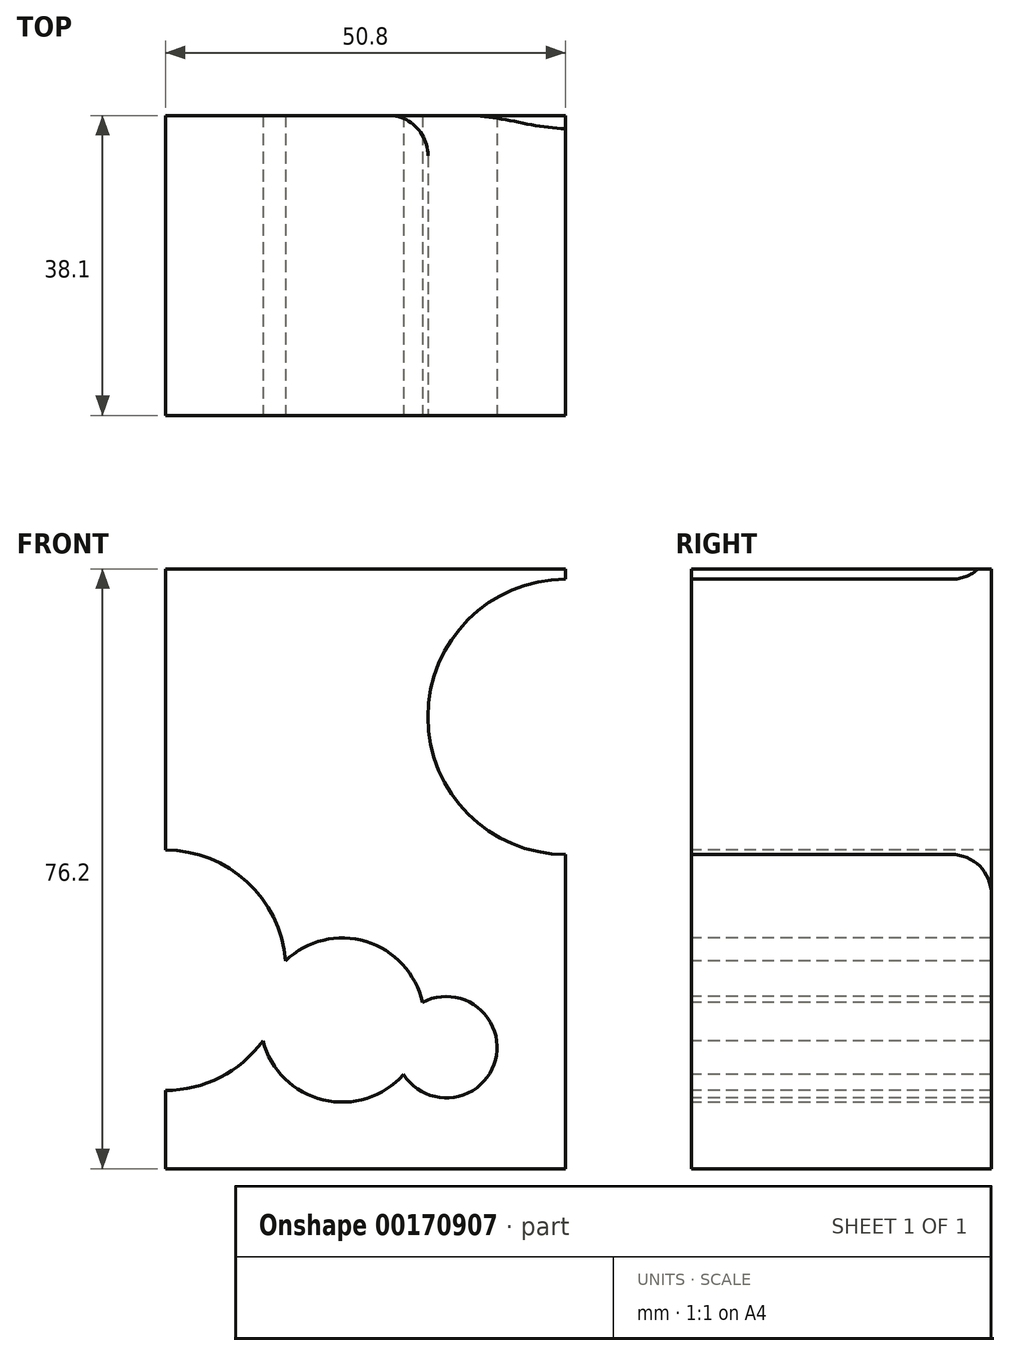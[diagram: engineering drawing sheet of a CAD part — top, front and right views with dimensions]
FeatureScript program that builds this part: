
annotation { "Feature Type Name" : "Feature", "Feature Type Description" : "" }
export const myFeature = defineFeature(function(context is Context, id is Id, definition is map)
    precondition{}
    {
        {
            var Q0;
            Q0=qCreatedBy(makeId("Top.planeOp"),FACE);
            var sketch = newSketch(context, id + "F0", { "sketchPlane" : qUnion([Q0])});
            skLineSegment(sketch, "E0.bottom", {"start": v(-50.8, 12.7) * mm, "end": v(0, 12.7) * mm});
            skLineSegment(sketch, "E0.top", {"start": v(-50.8, -25.4) * mm, "end": v(0, -25.4) * mm});
            skLineSegment(sketch, "E0.left", {"start": v(-50.8, 12.7) * mm, "end": v(-50.8, -25.4) * mm});
            skLineSegment(sketch, "E0.right", {"start": v(0, 12.7) * mm, "end": v(0, -25.4) * mm});
            skSolve(sketch);
        }
        {
            var Q0;
            Q0=makeQuery(id+"F0.imprint","IMPRINT",FACE,{"disambiguationData":[TD([[makeQuery(id+"F0.imprint","IMPRINT",EDGE,{"derivedFrom":sQuery(id+"F0.wireOp",EDGE,"E0.bottom")}),-1.0]])]});
            extrude(context, id + "F1", {"entities" : qUnion([Q0]), "depth" : 76.2 * mm});
        }
        {
            var Q0;
            Q0=makeQuery(id+"F1.opExtrude","SWEPT_FACE",FACE,{"disambiguationData":[OSD([sQuery(id+"F0.wireOp",EDGE,"E0.top")])]});
            var sketch = newSketch(context, id + "F2", { "sketchPlane" : qUnion([Q0])});
            skCircle(sketch, "E1", {"center": v(-50.8, 25.2) * mm, "radius": 15.27 * mm});
            skCircle(sketch, "E2", {"center": v(0, 57.4) * mm, "radius": 17.48 * mm});
            skCircle(sketch, "E3", {"center": v(-28.36, 18.88) * mm, "radius": 10.43 * mm});
            skCircle(sketch, "E4", {"center": v(-15.14, 15.43) * mm, "radius": 6.44 * mm});
            skSolve(sketch);
        }
        {
            var Q0;
            Q0 = qSketchRegion(id + "F2", true);
            extrude(context, id + "F3", {"entities" : qUnion([Q0]), "operationType" : NewBodyOperationType.REMOVE, "endBound" : BoundingType.THROUGH_ALL, "oppositeDirection" : true, "depth" : 25.4 * mm});
        }
        {
            var Q0;
            Q0=makeQuery(id+"F3.boolean.opBoolean","INTERSECT",EDGE,{"derivedFrom":[makeQuery(id+"F1.opExtrude","SWEPT_FACE",FACE,{"disambiguationData":[OSD([sQuery(id+"F0.wireOp",EDGE,"E0.bottom")])]}),makeQuery(id+"F3.opExtrude","SWEPT_FACE",FACE,{"disambiguationData":[OSD([sQuery(id+"F2.wireOp",EDGE,"E2")])]})]});
            fillet(context, id + "F4", {"entities" : qUnion([Q0]), "tangentPropagation" : true, "radius" : 5.08 * mm, "defaultsChanged" : false, "vertexSettings" : [], "allowEdgeOverflow" : false});
        }
    });
